# Revit family: Hager-VOLTA-Surface_mounted-IP30-Without_Cover-Without_DIN-NoHosted-CH-it
name_source: partatom
category: Electrical Equipment
units: mm (PartAtom-declared; Revit-internal decimal feet)

## family parameters
Always vertical = Yes
Cut with Voids When Loaded = No
Maintain Annotation Orientation = No
Panel Configuration = Two Columns, Circuits Across
Part Type = Panelboard
Room Calculation Point = No
Round Connector Dimension = Use Diameter
Shared = No
Work Plane-Based = Yes

## types (1)
- VOLTA-Surface_mounted_W305_H640_D96_12_Modular_Spacing-VA48MD
    BC_METADATA = {"ObjectGuid":"bc35c96e-cb38-443e-833d-0616858cb9ac","ModelGuid":"8af03f69-2293-4735-a617-cc53adf55621","VariantGuid":"8b6e323b-1b53-409a-a940-11b5a7fc5337","Revision":"#4","VariantName":"Template-Enclosure_EU-EC000214"}
    BC_MODEL_ID = 1547145
    BC_OBJECT_ID = 513473
    BC_OBJECT_VERSION = #9
    BC_VARIANT_ID = 1174158
    Code hager = ADD-EC000214_EU
    Default Elevation = 1200 mm
    EF000003 - modo di montaggio = apparente
    EF000007 - colore = bianco
    EF000008 - larghezza = 305 mm  [stored 1.00066 ft]
    EF000024 - resistente ai raggi UV = No
    EF000040 - altezza = 640 mm  [stored 2.09974 ft]
    EF000049 - profondità = 96 mm  [stored 0.314961 ft]
    EF000116 - numero RAL = 9010
    EF000118 - con piastra di montaggio = Yes
    EF000218 - profondità di montaggio = 0 mm  [stored 0 ft]
    EF000266 - numero di file = 4
    EF000332 - altezza di installazione = 0 mm  [stored 0 ft]
    EF000846 - larghezza di montaggio = 0 mm  [stored 0 ft]
    EF001062 - versione EMC = No
    EF001088 - possibilità di applicazione = Yes
    EF001131 - profondità interna = 0 mm  [stored 0 ft]
    EF001134 - barra DIN = No
    EF002950 - numero di unità modulari = 12
    EF005474 - grado di protezione (IP) = IP30
    EF006244 - coperchio/porta trasparente = No
    EF006306 - con serratura = No
    EF009212 - tipo di coperchio = con taglio
    EF015776 - morsetto di messa a terra = No
    EF015777 - morsettiera a conduttore neutro = No
    EF015941 - porta di trasmissione del segnale = No
    ETIM class code = EC000214
    ETIM class name = Small distribution board
    HG000001 - Numero di colonne = 0
    HG000002-with door or cover-it = No
    HG000003-Range-it = VOLTA
    HG000004-Manufacturer reference-it = VA48MD
    HG000005-Thickness-it = 2 mm  [stored 0.00656168 ft]
    HG000006-Flush mounted-it = No
    HG000007-Number of empty columns-it = 0
    HG000008-Number of empty rows-it = 0
    HG000009-Double swing door-it = No
    HG000010-Asymmetric doors-it = No
    HG000011-Empty rows from bottom-it = No
    HG000012-Door swing angle-it = 90.00°
    HG000013-Door on the left-it = No
    HG000014-Door on the right-it = Yes
    HG000015-Clearance visibility-it = Yes
    HG000016-Door 3D visibility-it = Yes
    HG000017-Distance between poles-it = 18 mm  [stored 0.0590551 ft]
    HG000060-RAL-number = 9010
    HG000099-Onfly Template ID-it-CH = 507532
    HGEF000266-Numero di file = 4
    HGEF0002950-larghezza in unità di suddivisione = 12
    Manufacturer = Hager
    Name = VOLTA-Surface_mounted-IP30-Without_Cover-Without_DIN-CH
    Name BIM&CO = Electricity
    Name hager = ADD_Enclosures_EC000214
    Reference = VOLTA-Surface_mounted_W305_H640_D96_12_Modular_Spacing-VA48MD
    Uniformat = Low Tension Service & Dist.
    Uniformat code = D501001

note: [stored X ft] marks values corroborated as IEEE doubles in the binary element streams (Revit-internal decimal feet)

## geometry (parser evidence)
native form markers: Sweep x15
no freeform markers — native parametric forms only
